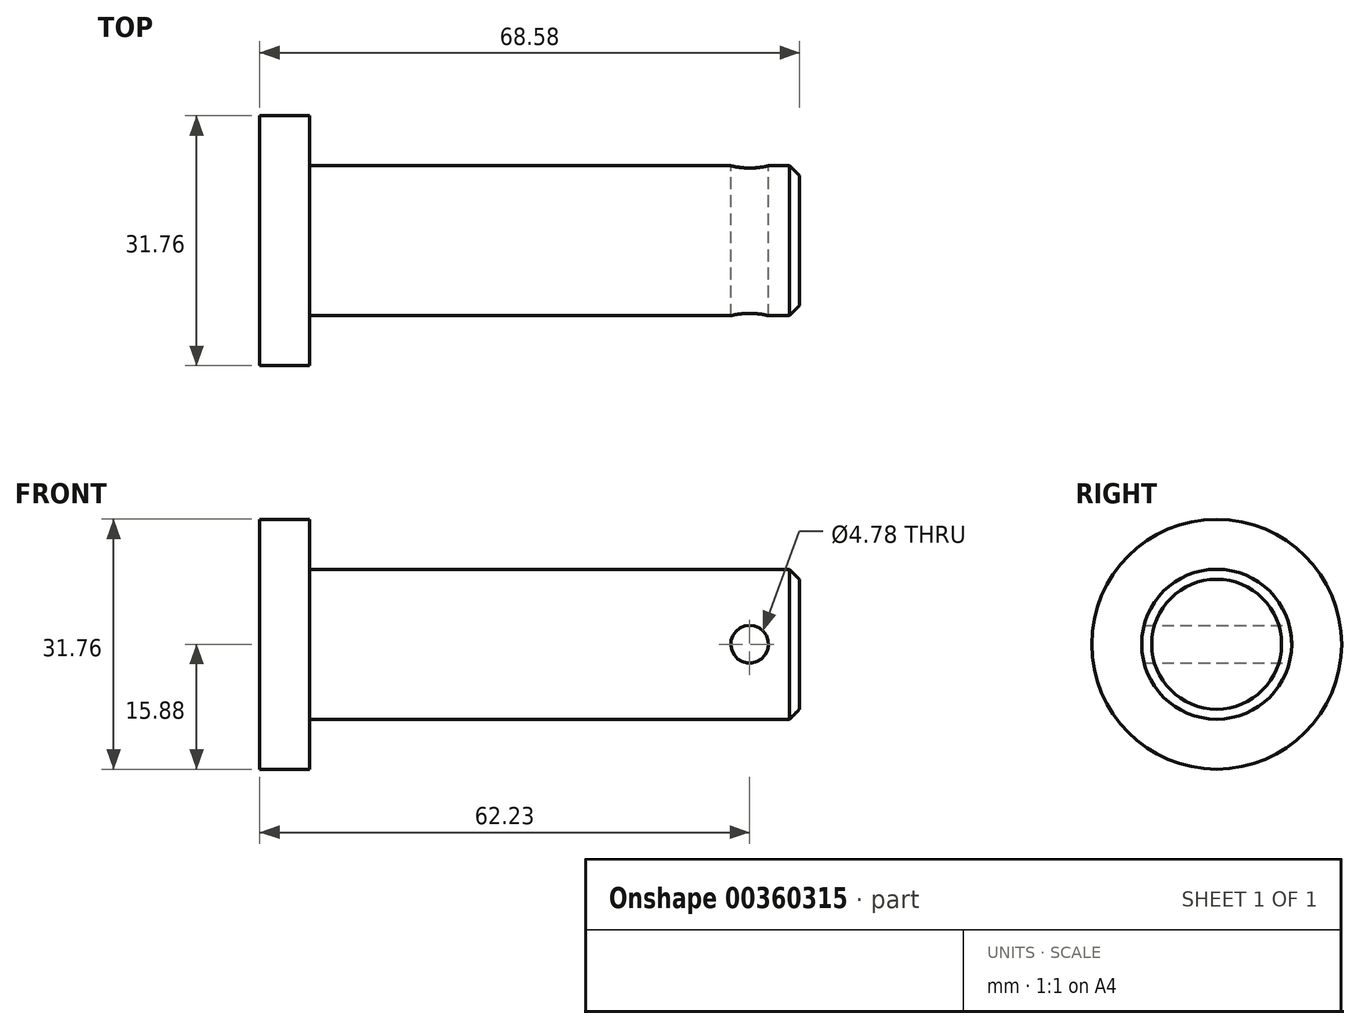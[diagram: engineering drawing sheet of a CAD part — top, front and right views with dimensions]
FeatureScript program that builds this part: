
annotation { "Feature Type Name" : "Feature", "Feature Type Description" : "" }
export const myFeature = defineFeature(function(context is Context, id is Id, definition is map)
    precondition{}
    {
        {
            var Q0;
            Q0=qCreatedBy(makeId("Right.planeOp"),FACE);
            var sketch = newSketch(context, id + "F0", { "sketchPlane" : qUnion([Q0])});
            skCircle(sketch, "E0", {"center": v(0, 0) * mm, "radius": 15.88 * mm});
            skSolve(sketch);
        }
        {
            var Q0;
            Q0 = qSketchRegion(id + "F0", true);
            extrude(context, id + "F1", {"entities" : qUnion([Q0]), "depth" : 6.35 * mm});
        }
        {
            var Q0;
            Q0=makeQuery(id+"F1.opExtrude","CAP_FACE",FACE,{"disambiguationData":[OSD([sQuery(id+"F0.wireOp",EDGE,"E0")])],"isStart":false});
            var sketch = newSketch(context, id + "F2", { "sketchPlane" : qUnion([Q0])});
            skCircle(sketch, "E1", {"center": v(0, 0) * mm, "radius": 9.53 * mm});
            skSolve(sketch);
        }
        {
            var Q0;
            Q0 = qSketchRegion(id + "F2", true);
            extrude(context, id + "F3", {"entities" : qUnion([Q0]), "operationType" : NewBodyOperationType.ADD, "depth" : 62.23 * mm});
        }
        {
            var Q0;
            Q0=makeQuery(id+"F3.opExtrude","CAP_EDGE",EDGE,{"disambiguationData":[OSD([sQuery(id+"F2.wireOp",EDGE,"E1")])],"isStart":false});
            chamfer(context, id + "F4", {"entities" : qUnion([Q0]), "chamferType" : ChamferType.OFFSET_ANGLE, "width" : 1.27 * mm, "oppositeDirection" : false, "angle" : 45 * degree, "tangentPropagation" : true});
        }
        {
            var Q0;
            Q0=qCreatedBy(makeId("Front.planeOp"),FACE);
            var sketch = newSketch(context, id + "F5", { "sketchPlane" : qUnion([Q0])});
            skCircle(sketch, "E2", {"center": v(62.23, 0) * mm, "radius": 2.39 * mm});
            skSolve(sketch);
        }
        {
            var Q0;
            Q0 = qSketchRegion(id + "F5", true);
            extrude(context, id + "F6", {"entities" : qUnion([Q0]), "operationType" : NewBodyOperationType.REMOVE, "depth" : 51.3 * mm, "hasSecondDirection" : true, "secondDirectionOppositeDirection" : true, "secondDirectionDepth" : 25.4 * mm});
        }
    });
